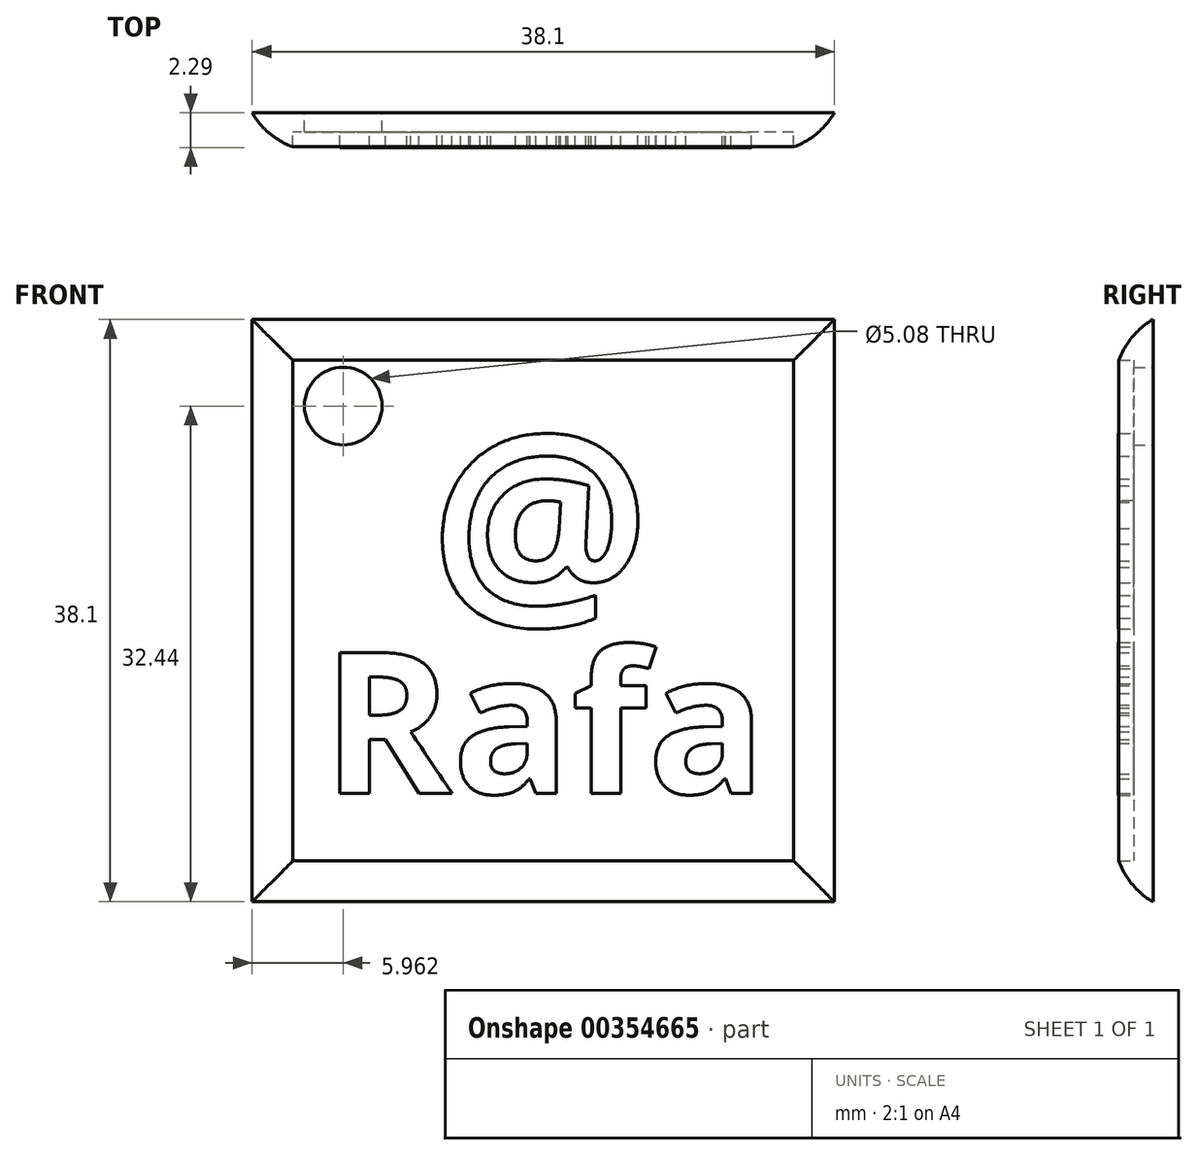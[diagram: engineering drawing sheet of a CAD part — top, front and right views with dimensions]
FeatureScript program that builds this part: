
annotation { "Feature Type Name" : "Feature", "Feature Type Description" : "" }
export const myFeature = defineFeature(function(context is Context, id is Id, definition is map)
    precondition{}
    {
        {
            var Q0;
            Q0=qCreatedBy(makeId("Front.planeOp"),FACE);
            var sketch = newSketch(context, id + "F0", { "sketchPlane" : qUnion([Q0])});
            skLineSegment(sketch, "E0.bottom", {"start": v(-19.05, 19.05) * mm, "end": v(19.05, 19.05) * mm});
            skLineSegment(sketch, "E0.top", {"start": v(-19.05, -19.05) * mm, "end": v(19.05, -19.05) * mm});
            skLineSegment(sketch, "E0.left", {"start": v(-19.05, 19.05) * mm, "end": v(-19.05, -19.05) * mm});
            skLineSegment(sketch, "E0.right", {"start": v(19.05, 19.05) * mm, "end": v(19.05, -19.05) * mm});
            skPoint(sketch, "E0.middle", {"position": v(0, 0) * mm});
            skLineSegment(sketch, "E1.bottom", {"start": v(16.39, 16.39) * mm, "end": v(-16.39, 16.39) * mm});
            skLineSegment(sketch, "E1.top", {"start": v(16.39, -16.39) * mm, "end": v(-16.39, -16.39) * mm});
            skLineSegment(sketch, "E1.left", {"start": v(16.39, 16.39) * mm, "end": v(16.39, -16.39) * mm});
            skLineSegment(sketch, "E1.right", {"start": v(-16.39, 16.39) * mm, "end": v(-16.39, -16.39) * mm});
            skSolve(sketch);
        }
        {
            var Q0;
            Q0=makeQuery(id+"F0.imprint","IMPRINT",FACE,{"disambiguationData":[TD([[makeQuery(id+"F0.imprint","IMPRINT",EDGE,{"derivedFrom":sQuery(id+"F0.wireOp",EDGE,"E0.bottom")}),-1.0]])]});
            extrude(context, id + "F1", {"entities" : qUnion([Q0]), "depth" : 2.54 * mm});
        }
        {
            var Q0;
            Q0=makeQuery(id+"F0.imprint","IMPRINT",FACE,{"disambiguationData":[TD([[makeQuery(id+"F0.imprint","IMPRINT",EDGE,{"derivedFrom":sQuery(id+"F0.wireOp",EDGE,"E1.bottom")}),1.0]])]});
            extrude(context, id + "F2", {"entities" : qUnion([Q0]), "operationType" : NewBodyOperationType.ADD, "depth" : 1.27 * mm});
        }
        {
            var Q0;
            Q0=makeQuery(id+"F1.opExtrude","CAP_EDGE",EDGE,{"disambiguationData":[OSD([sQuery(id+"F0.wireOp",EDGE,"E0.bottom")])],"isStart":false});
            var Q1;
            Q1=makeQuery(id+"F1.opExtrude","CAP_EDGE",EDGE,{"disambiguationData":[OSD([sQuery(id+"F0.wireOp",EDGE,"E0.left")])],"isStart":false});
            var Q2;
            Q2=makeQuery(id+"F1.opExtrude","CAP_EDGE",EDGE,{"disambiguationData":[OSD([sQuery(id+"F0.wireOp",EDGE,"E0.top")])],"isStart":false});
            var Q3;
            Q3=makeQuery(id+"F1.opExtrude","CAP_EDGE",EDGE,{"disambiguationData":[OSD([sQuery(id+"F0.wireOp",EDGE,"E0.right")])],"isStart":false});
            fillet(context, id + "F3", {"entities" : qUnion([Q0, Q1, Q2, Q3]), "radius" : 5.08 * mm, "tangentPropagation" : true, "allowEdgeOverflow" : false});
        }
        {
            var Q0;
            Q0=qCreatedBy(makeId("Front.planeOp"),FACE);
            var sketch = newSketch(context, id + "F4", { "sketchPlane" : qUnion([Q0])});
            skCircle(sketch, "E2", {"center": v(-13.09, 13.4) * mm, "radius": 2.54 * mm});
            skSolve(sketch);
        }
        {
            var Q0;
            Q0=makeQuery(id+"F4.imprint","IMPRINT",FACE,{"disambiguationData":[TD([[makeQuery(id+"F4.imprint","IMPRINT",EDGE,{"derivedFrom":sQuery(id+"F4.wireOp",EDGE,"E2")}),1.0]])]});
            extrude(context, id + "F5", {"entities" : qUnion([Q0]), "operationType" : NewBodyOperationType.REMOVE, "depth" : 25.4 * mm});
        }
        {
            var Q0;
            Q0=qCreatedBy(makeId("Front.planeOp"),FACE);
            var sketch = newSketch(context, id + "F6", { "sketchPlane" : qUnion([Q0])});
            skText(sketch, "E3", { "text": "@", "fontName": "OpenSans-Bold.ttf"});
            skText(sketch, "E4", { "text": "Rafa", "fontName": "OpenSans-Bold.ttf"});
            const initialGuessF6  = {"E3": [-0.0074, 0, 1, 0, 0.01155], "E4": [-0.01447, -0.01195, 1, 0, 0.00928]};
            skSetInitialGuess(sketch, initialGuessF6);
            skSolve(sketch);
        }
        {
            var Q0;
            Q0 = qSketchRegion(id + "F6", true);
            extrude(context, id + "F7", {"entities" : qUnion([Q0]), "operationType" : NewBodyOperationType.ADD, "depth" : 2.3 * mm});
        }
    });
